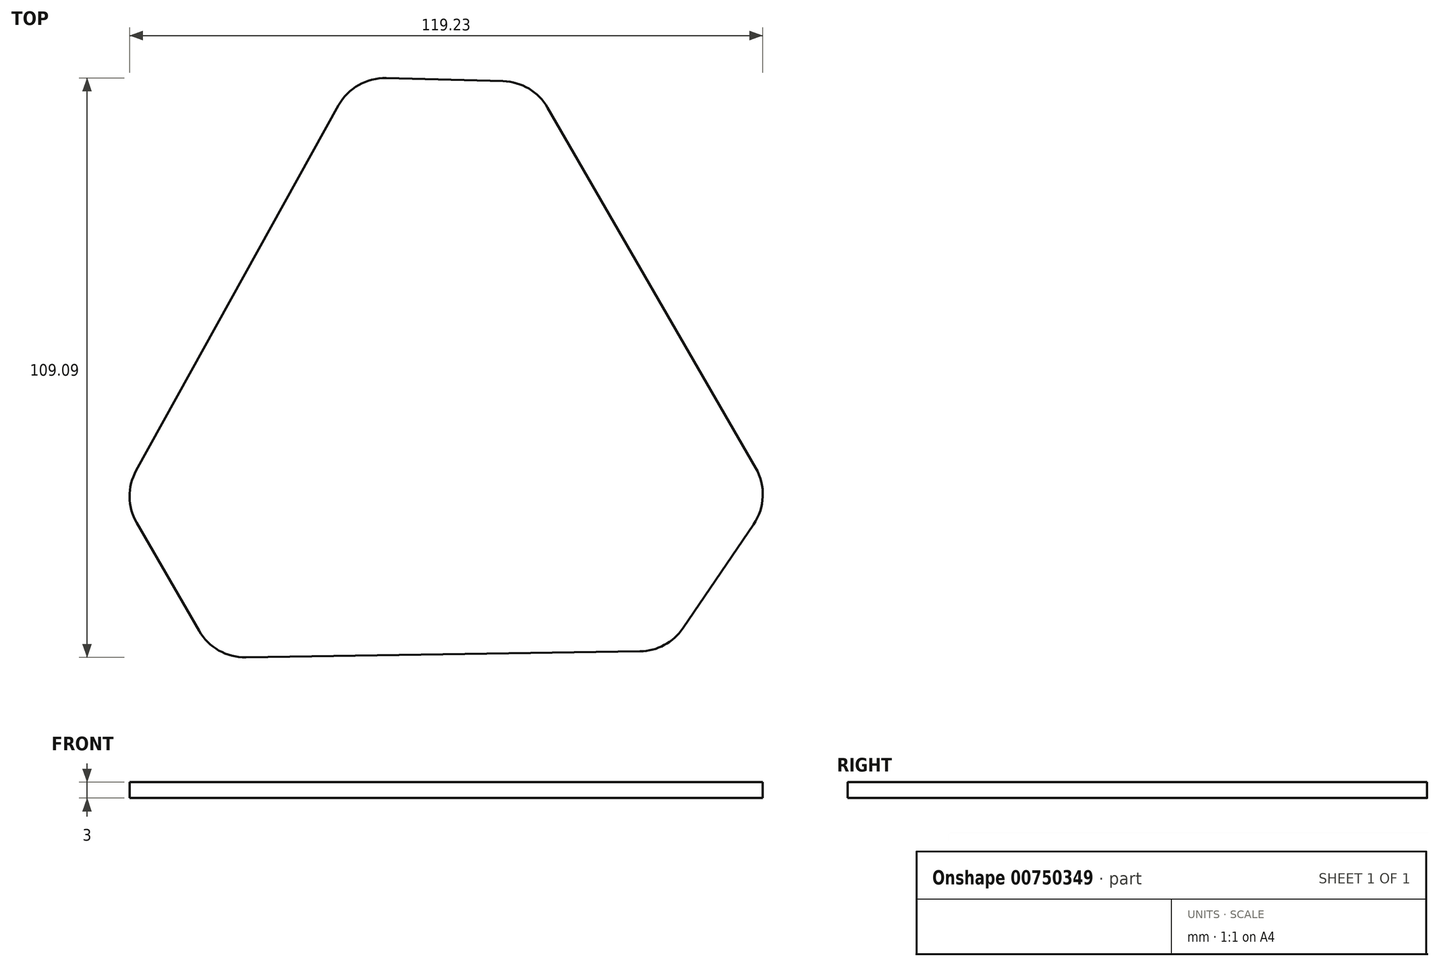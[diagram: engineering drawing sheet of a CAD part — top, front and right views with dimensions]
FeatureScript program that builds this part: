
annotation { "Feature Type Name" : "Feature", "Feature Type Description" : "" }
export const myFeature = defineFeature(function(context is Context, id is Id, definition is map)
    precondition{}
    {
        {
            var Q0;
            Q0=qCreatedBy(makeId("Top.planeOp"),FACE);
            var sketch = newSketch(context, id + "F0", { "sketchPlane" : qUnion([Q0])});
            skCircle(sketch, "E0.cCircle", {"center": v(0, 0) * mm, "radius": 60.62 * mm, "construction": true});
            skLineSegment(sketch, "E0.1", {"start": v(35, 60.62) * mm, "end": v(70, 0) * mm, "construction": true});
            skLineSegment(sketch, "E0.3", {"start": v(35, -60.62) * mm, "end": v(-35, -60.62) * mm, "construction": true});
            skLineSegment(sketch, "E0.5", {"start": v(-70, 0) * mm, "end": v(-35, 60.62) * mm, "construction": true});
            skPoint(sketch, "E0.0.midPoint", {"position": v(0, 60.62) * mm});
            skLineSegment(sketch, "E1", {"start": v(0, 0) * mm, "end": v(-127.23, -73.46) * mm, "construction": true});
            skLineSegment(sketch, "E2", {"start": v(0, 0) * mm, "end": v(0, 106.04) * mm, "construction": true});
            skLineSegment(sketch, "E3", {"start": v(0, 0) * mm, "end": v(125.66, -72.55) * mm, "construction": true});
            skLineSegment(sketch, "E4", {"start": v(-120.23, -49.2) * mm, "end": v(-17.5, 10.1) * mm, "construction": true});
            skLineSegment(sketch, "E5.MirrorCS", {"start": v(-102.73, -79.52) * mm, "end": v(0, -20.2) * mm, "construction": true});
            skLineSegment(sketch, "E6", {"start": v(-17.5, 103.57) * mm, "end": v(-17.5, 10.1) * mm, "construction": true});
            skLineSegment(sketch, "E7.MirrorCS", {"start": v(17.5, 103.57) * mm, "end": v(17.5, 10.1) * mm, "construction": true});
            skLineSegment(sketch, "E8", {"start": v(-20.44, 58.56) * mm, "end": v(-58.53, -10.22) * mm});
            skLineSegment(sketch, "E9.1.0", {"start": v(102.73, -79.52) * mm, "end": v(0, -20.2) * mm, "construction": true});
            skLineSegment(sketch, "E9.1.1", {"start": v(120.23, -49.2) * mm, "end": v(17.5, 10.1) * mm, "construction": true});
            skLineSegment(sketch, "E10", {"start": v(18.94, 58.12) * mm, "end": v(58.11, -9.72) * mm});
            skLineSegment(sketch, "E11", {"start": v(-58.44, -20.07) * mm, "end": v(-46.69, -40.39) * mm});
            skPoint(sketch, "E12.visualSharp", {"position": v(-61.27, -15.17) * mm});
            skArc(sketch, "E12.filletArc", {"start": v(-58.53, -10.22) * mm, "mid": v(-59.78, -15.16) * mm, "end": v(-58.44, -20.07) * mm});
            skLineSegment(sketch, "E13", {"start": v(57.72, -20.34) * mm, "end": v(44.44, -39.88) * mm});
            skLineSegment(sketch, "E14", {"start": v(-37.88, -45.38) * mm, "end": v(36.32, -44.25) * mm});
            skPoint(sketch, "E15.visualSharp", {"position": v(-43.75, -45.47) * mm});
            skArc(sketch, "E15.filletArc", {"start": v(-46.69, -40.39) * mm, "mid": v(-42.96, -44.08) * mm, "end": v(-37.88, -45.38) * mm});
            skPoint(sketch, "E16.visualSharp", {"position": v(41.51, -44.18) * mm});
            skArc(sketch, "E16.filletArc", {"start": v(36.32, -44.25) * mm, "mid": v(40.91, -43.06) * mm, "end": v(44.44, -39.88) * mm});
            skPoint(sketch, "E17.visualSharp", {"position": v(61.25, -15.16) * mm});
            skArc(sketch, "E17.filletArc", {"start": v(57.72, -20.34) * mm, "mid": v(59.45, -15.09) * mm, "end": v(58.11, -9.72) * mm});
            skLineSegment(sketch, "E18", {"start": v(-11.43, 63.7) * mm, "end": v(10.55, 63.12) * mm});
            skPoint(sketch, "E19.visualSharp", {"position": v(-17.5, 63.87) * mm});
            skArc(sketch, "E19.filletArc", {"start": v(-11.43, 63.7) * mm, "mid": v(-16.66, 62.4) * mm, "end": v(-20.44, 58.56) * mm});
            skPoint(sketch, "E20.visualSharp", {"position": v(16.15, 62.97) * mm});
            skArc(sketch, "E20.filletArc", {"start": v(18.94, 58.12) * mm, "mid": v(15.4, 61.71) * mm, "end": v(10.55, 63.12) * mm});
            skSolve(sketch);
        }
        {
            var Q0;
            Q0=makeQuery(id+"F0.imprint","IMPRINT",FACE,{"disambiguationData":[TD([[makeQuery(id+"F0.imprint","IMPRINT",EDGE,{"derivedFrom":sQuery(id+"F0.wireOp",EDGE,"E8")}),1.0]])]});
            extrude(context, id + "F1", {"entities" : qUnion([Q0]), "depth" : 3 * mm, "offsetDistance" : 25 * mm});
        }
    });
